# Revit family: Cabina mural para agua nebulizada_Aguilera Extincion
name_source: partatom
category: Equipos mecánicos
revit_build: Autodesk Revit 2017 (Build: 20160225_1515(x64)
units: mm (PartAtom-declared; Revit-internal decimal feet)

## family parameters
Anfitrión = Muro
Compartido = No
Corte con vacíos al cargar = No
Cota de conector redondo = Radio de uso
Número OmniClass = 23.65.70.17.11.27
Punto de cálculo de habitación = No
Siempre vertical = Sí
Tipo de pieza = Normal
Título OmniClass = Cabinets for Fire Hoses

## types (1)
- Cabina mural para agua nebulizada
    Alto = 600 mm
    Ancho = 800 mm  [stored 2.62467 ft]
    Comentarios de tipo = Cabina  montaje  mural  disponible  en  dos terminaciones: Acero al carbono 1.5 mm espesor pintada al horno (RAL 3000); Acero inoxidable AISI-304. Dimensiones (alto-ancho-fondo): 600 X 800 X 240. Carrete axial recogida automática. Manguera 3/8”. Longitud 25 m  (consultar para otras longitudes). Boquilla: Dispone de 4 difusores direccionales centrales y 8 laterales. Caudal variable entre 11/25 litros por minuto según modelo. Presión pruebas:  330 bar. Presión trabajo:   140 bar. Rápida respuesta ante un conato de incendio, atacándolo desde el origen del mismo. Reducido consumo de agua. Instalación sencilla. Los daños producidos por el agua se minimizan.
    D manguera = 10 mm  [stored 0.0328084 ft]
    Descripción = Boca de incendio para sistemas de agua nebulizada de alta presión Microaqua de Aguilera Extinción. Se compone de un armario mural donde se aloja una lanza para  agua  nebulizada  y  un  carrete  axial  con  recogida  automática. Lanza de agua nebulizada especialmente diseñada para la lucha contra fuegos manualmente desde el propio origen del mismo. El diseño de la lanza proporciona una lucha eficaz contra el fuego y una protección al usuario de la misma, creando una cortina nebulizadora que le protege del fuego. Válido para aquellas aplicaciones donde por razones técnicas o económicas no es posible realizar una instalación fija de difusores.
    Fabricante = Aguilera Extinción
    Flujo máximo = 11.0 L/min
    Flujo mínimo = 25.0 L/min
    Fondo = 240 mm  [stored 0.787402 ft]
    Modelo = AN/CM1
    Presión pruebas = 330.0 Pa
    Presión trabajo = 140.0 Pa
    Rt = 5 mm
    Símbolo = Sí
    Símbolo texto modelo = Sí
    URL = http://aguilera.es

note: [stored X ft] marks values corroborated as IEEE doubles in the binary element streams (Revit-internal decimal feet)
